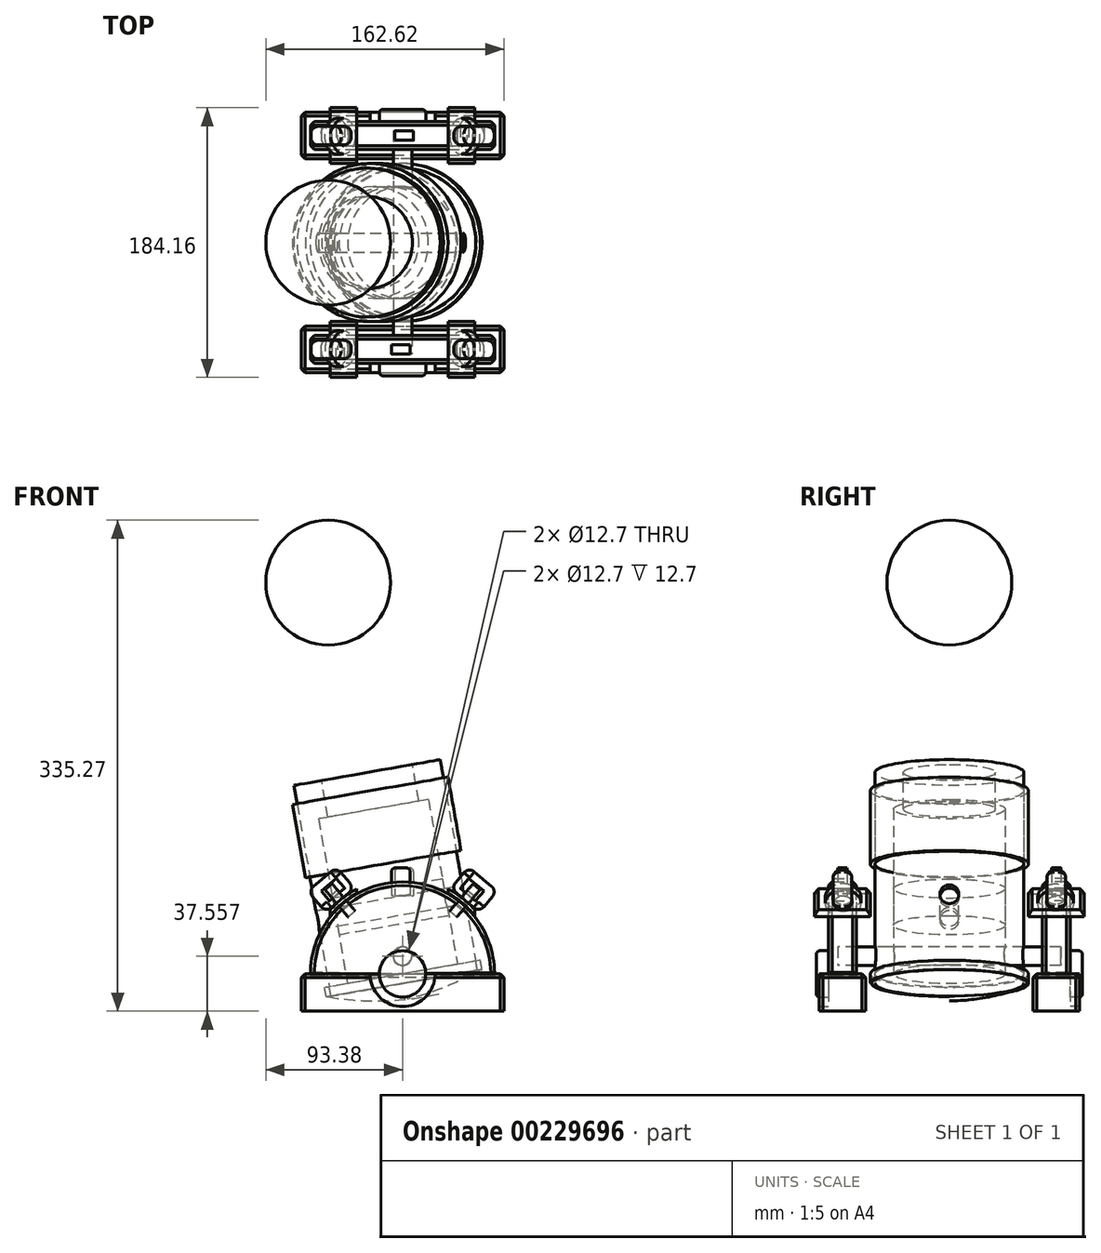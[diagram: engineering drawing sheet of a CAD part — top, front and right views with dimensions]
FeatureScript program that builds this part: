
annotation { "Feature Type Name" : "Feature", "Feature Type Description" : "" }
export const myFeature = defineFeature(function(context is Context, id is Id, definition is map)
    precondition{}
    {
        {
            var Q0;
            Q0=qCreatedBy(makeId("Top.planeOp"),FACE);
            var sketch = newSketch(context, id + "F0", { "sketchPlane" : qUnion([Q0])});
            skCircle(sketch, "E0", {"center": v(0, 0) * mm, "radius": 38.1 * mm});
            skCircle(sketch, "E1", {"center": v(0, 0) * mm, "radius": 50.8 * mm});
            skSolve(sketch);
        }
        {
            var Q0;
            Q0=makeQuery(id+"F0.imprint","IMPRINT",FACE,{"disambiguationData":[TD([[makeQuery(id+"F0.imprint","IMPRINT",EDGE,{"derivedFrom":sQuery(id+"F0.wireOp",EDGE,"E0")}),-1.0]])]});
            extrude(context, id + "F1", {"entities" : qUnion([Q0]), "depth" : 139.7 * mm});
        }
        {
            var Q0;
            Q0=qCreatedBy(makeId("Top.planeOp"),FACE);
            cPlane(context, id + "F2", {"entities" : qUnion([Q0]), "cplaneType" : CPlaneType.OFFSET, "offset" : 76.2 * mm, "width" : 152.4 * mm, "height" : 152.4 * mm});
        }
        {
            var Q0;
            Q0=qCreatedBy(id+"F2.planeOp",FACE);
            var sketch = newSketch(context, id + "F3", { "sketchPlane" : qUnion([Q0])});
            skCircle(sketch, "E2", {"center": v(0, 0) * mm, "radius": 50.8 * mm});
            skCircle(sketch, "E3", {"center": v(0, 0) * mm, "radius": 53.98 * mm});
            skSolve(sketch);
        }
        {
            var Q0;
            Q0=makeQuery(id+"F3.imprint","IMPRINT",FACE,{"disambiguationData":[TD([[makeQuery(id+"F3.imprint","IMPRINT",EDGE,{"derivedFrom":sQuery(id+"F3.wireOp",EDGE,"E2")}),-1.0]])]});
            extrude(context, id + "F4", {"entities" : qUnion([Q0]), "depth" : 50.8 * mm});
        }
        {
            var Q0;
            Q0=qCreatedBy(makeId("Front.planeOp"),FACE);
            cPlane(context, id + "F5", {"entities" : qUnion([Q0]), "cplaneType" : CPlaneType.OFFSET, "offset" : 63.5 * mm, "width" : 152.4 * mm, "height" : 152.4 * mm});
        }
        {
            var Q0;
            Q0=qCreatedBy(id+"F5.planeOp",FACE);
            var sketch = newSketch(context, id + "F6", { "sketchPlane" : qUnion([Q0])});
            skArc(sketch, "E4", {"start": v(45.28, -43.66) * mm, "mid": v(43.66, 45.28) * mm, "end": v(-45.28, 43.66) * mm});
            skLineSegment(sketch, "E5", {"start": v(-45.28, 43.66) * mm, "end": v(45.28, -43.66) * mm});
            skSolve(sketch);
        }
        {
            var Q0;
            Q0 = qSketchRegion(id + "F6", true);
            extrude(context, id + "F7", {"entities" : qUnion([Q0]), "depth" : 19.05 * mm});
        }
        {
            var Q0;
            Q0=qCreatedBy(makeId("Top.planeOp"),FACE);
            var sketch = newSketch(context, id + "F8", { "sketchPlane" : qUnion([Q0])});
            skLineSegment(sketch, "E6", {"start": v(0, 0) * mm, "end": v(0, -70.78) * mm});
            skSolve(sketch);
        }
        {
            var Q0;
            Q0=makeQuery(id+"F7.opExtrude","SWEPT_BODY",BODY,{"disambiguationData":[OSD([sQuery(id+"F6.wireOp",EDGE,"E4"),sQuery(id+"F6.wireOp",EDGE,"E5")])]});
            var Q1;
            Q1=sQuery(id+"F8.wireOp",EDGE,"E6");
            transform(context, id + "F9", {"entities" : qUnion([Q0]), "transformType" : TransformType.ROTATION, "transformAxis" : qUnion([Q1]), "angle" : 45 * degree, "makeCopy" : false});
        }
        {
            var Q0;
            Q0=qCreatedBy(makeId("Top.planeOp"),FACE);
            var sketch = newSketch(context, id + "F10", { "sketchPlane" : qUnion([Q0])});
            skLineSegment(sketch, "E7.0.0", {"start": v(-62.9, -63.5) * mm, "end": v(62.9, -63.5) * mm});
            skLineSegment(sketch, "E7.0.1", {"start": v(62.9, -63.5) * mm, "end": v(62.9, -82.55) * mm});
            skLineSegment(sketch, "E7.0.2", {"start": v(62.9, -82.55) * mm, "end": v(-62.9, -82.55) * mm});
            skLineSegment(sketch, "E7.0.3", {"start": v(-62.9, -82.55) * mm, "end": v(-62.9, -63.5) * mm});
            skLineSegment(sketch, "E8", {"start": v(-62.9, -82.55) * mm, "end": v(-69.24, -82.55) * mm});
            skLineSegment(sketch, "E9", {"start": v(-62.9, -82.55) * mm, "end": v(-62.9, -88.9) * mm});
            skLineSegment(sketch, "E10.MirrorCS", {"start": v(62.9, -82.55) * mm, "end": v(62.9, -88.9) * mm});
            skLineSegment(sketch, "E11.MirrorCS", {"start": v(62.9, -82.55) * mm, "end": v(69.24, -82.55) * mm});
            skLineSegment(sketch, "E12", {"start": v(62.9, -63.5) * mm, "end": v(62.9, -57.15) * mm});
            skLineSegment(sketch, "E13", {"start": v(62.9, -63.5) * mm, "end": v(69.24, -63.5) * mm});
            skLineSegment(sketch, "E14.bottom", {"start": v(-69.24, -88.9) * mm, "end": v(69.24, -88.9) * mm});
            skLineSegment(sketch, "E14.top", {"start": v(-69.24, -57.15) * mm, "end": v(69.24, -57.15) * mm});
            skLineSegment(sketch, "E14.left", {"start": v(-69.24, -88.9) * mm, "end": v(-69.24, -57.15) * mm});
            skLineSegment(sketch, "E14.right", {"start": v(69.24, -88.9) * mm, "end": v(69.24, -57.15) * mm});
            skSolve(sketch);
        }
        {
            var Q0;
            {var subQ0=sQuery(id+"F10.wireOp",EDGE,"E12");Q0=makeQuery(id+"F10.imprint","IMPRINT",FACE,{"disambiguationData":[TD([[makeQuery(id+"F10.imprint","IMPRINT",EDGE,{"derivedFrom":subQ0}),-1.0]])]});}
            var Q1;
            Q1=makeQuery(id+"F10.imprint","IMPRINT",FACE,{"disambiguationData":[TD([[makeQuery(id+"F10.imprint","IMPRINT",EDGE,{"derivedFrom":sQuery(id+"F10.wireOp",EDGE,"E7.0.1")}),1.0]])]});
            var Q2;
            Q2=makeQuery(id+"F10.imprint","IMPRINT",FACE,{"disambiguationData":[TD([[makeQuery(id+"F10.imprint","IMPRINT",EDGE,{"derivedFrom":sQuery(id+"F10.wireOp",EDGE,"E7.0.0")}),-1.0]])]});
            var Q3;
            Q3=makeQuery(id+"F10.imprint","IMPRINT",FACE,{"disambiguationData":[TD([[makeQuery(id+"F10.imprint","IMPRINT",EDGE,{"derivedFrom":sQuery(id+"F10.wireOp",EDGE,"E7.0.0")}),1.0]])]});
            var Q4;
            {var subQ0=sQuery(id+"F10.wireOp",EDGE,"E11.MirrorCS");Q4=makeQuery(id+"F10.imprint","IMPRINT",FACE,{"disambiguationData":[TD([[makeQuery(id+"F10.imprint","IMPRINT",EDGE,{"derivedFrom":subQ0}),-1.0]])]});}
            var Q5;
            Q5=makeQuery(id+"F10.imprint","IMPRINT",FACE,{"disambiguationData":[TD([[makeQuery(id+"F10.imprint","IMPRINT",EDGE,{"derivedFrom":sQuery(id+"F10.wireOp",EDGE,"E7.0.2")}),1.0]])]});
            var Q6;
            {var subQ0=sQuery(id+"F10.wireOp",EDGE,"E8");Q6=makeQuery(id+"F10.imprint","IMPRINT",FACE,{"disambiguationData":[TD([[makeQuery(id+"F10.imprint","IMPRINT",EDGE,{"derivedFrom":subQ0}),1.0]])]});}
            extrude(context, id + "F11", {"entities" : qUnion([Q0, Q1, Q2, Q3, Q4, Q5, Q6]), "oppositeDirection" : true, "depth" : 25.4 * mm});
        }
        {
            var Q0;
            Q0=makeQuery(id+"F7.opExtrude","CAP_FACE",FACE,{"disambiguationData":[OSD([sQuery(id+"F6.wireOp",EDGE,"E4"),sQuery(id+"F6.wireOp",EDGE,"E5")])],"isStart":false});
            var sketch = newSketch(context, id + "F12", { "sketchPlane" : qUnion([Q0])});
            skCircle(sketch, "E15", {"center": v(0, 0) * mm, "radius": 22.23 * mm});
            skCircle(sketch, "E16", {"center": v(0, 0) * mm, "radius": 15.88 * mm});
            skSolve(sketch);
        }
        {
            var Q0;
            {var subQ0=sQuery(id+"F12.wireOp",EDGE,"E16");var subQ1=makeQuery(id+"F7.opExtrude","CAP_EDGE",EDGE,{"disambiguationData":[OSD([sQuery(id+"F6.wireOp",EDGE,"E5")])],"isStart":false});var subQ2=makeQuery(id+"F12.imprint","INTERSECT",VERTEX,{"disambiguationData":[OD(0.0)],"derivedFrom":[subQ1,subQ0]});Q0=makeQuery(id+"F12.imprint","IMPRINT",FACE,{"disambiguationData":[TD([[makeQuery(id+"F12.imprint","IMPRINT",EDGE,{"disambiguationData":[TD([[subQ2,-1.0]])],"derivedFrom":subQ0}),1.0]])]});}
            var Q1;
            {var subQ0=sQuery(id+"F12.wireOp",EDGE,"E16");var subQ1=makeQuery(id+"F7.opExtrude","CAP_EDGE",EDGE,{"disambiguationData":[OSD([sQuery(id+"F6.wireOp",EDGE,"E5")])],"isStart":false});var subQ2=makeQuery(id+"F12.imprint","INTERSECT",VERTEX,{"disambiguationData":[OD(0.0)],"derivedFrom":[subQ1,subQ0]});Q1=makeQuery(id+"F12.imprint","IMPRINT",FACE,{"disambiguationData":[TD([[makeQuery(id+"F12.imprint","IMPRINT",EDGE,{"disambiguationData":[TD([[subQ2,1.0]])],"derivedFrom":subQ0}),1.0]])]});}
            extrude(context, id + "F13", {"entities" : qUnion([Q0, Q1]), "depth" : 8.38 * mm});
        }
        {
            var Q0;
            {var subQ0=sQuery(id+"F12.wireOp",EDGE,"E15");var subQ1=makeQuery(id+"F7.opExtrude","CAP_EDGE",EDGE,{"disambiguationData":[OSD([sQuery(id+"F6.wireOp",EDGE,"E5")])],"isStart":false});var subQ2=makeQuery(id+"F12.imprint","INTERSECT",VERTEX,{"disambiguationData":[OD(0.0)],"derivedFrom":[subQ1,subQ0]});Q0=makeQuery(id+"F12.imprint","IMPRINT",FACE,{"disambiguationData":[TD([[makeQuery(id+"F12.imprint","IMPRINT",EDGE,{"disambiguationData":[TD([[subQ2,-1.0]])],"derivedFrom":subQ0}),1.0]])]});}
            var Q1;
            {var subQ0=sQuery(id+"F12.wireOp",EDGE,"E15");var subQ1=makeQuery(id+"F7.opExtrude","CAP_EDGE",EDGE,{"disambiguationData":[OSD([sQuery(id+"F6.wireOp",EDGE,"E5")])],"isStart":false});var subQ2=makeQuery(id+"F12.imprint","INTERSECT",VERTEX,{"disambiguationData":[OD(0.0)],"derivedFrom":[subQ1,subQ0]});Q1=makeQuery(id+"F12.imprint","IMPRINT",FACE,{"disambiguationData":[TD([[makeQuery(id+"F12.imprint","IMPRINT",EDGE,{"disambiguationData":[TD([[subQ2,1.0]])],"derivedFrom":subQ0}),1.0]])]});}
            extrude(context, id + "F14", {"entities" : qUnion([Q0, Q1]), "depth" : 6.35 * mm});
        }
        {
            var Q0;
            Q0=makeQuery(id+"F14.opExtrude","CAP_EDGE",EDGE,{"disambiguationData":[OSD([sQuery(id+"F12.wireOp",EDGE,"E15")])],"isStart":false});
            var Q1;
            Q1=makeQuery(id+"F13.opExtrude","CAP_EDGE",EDGE,{"disambiguationData":[OSD([sQuery(id+"F12.wireOp",EDGE,"E16")])],"isStart":false});
            fillet(context, id + "F15", {"entities" : qUnion([Q0, Q1]), "radius" : 2.54 * mm, "tangentPropagation" : true, "allowEdgeOverflow" : false});
        }
        {
            var Q0;
            Q0 = qSketchRegion(id + "F12", true);
            var Q1;
            Q1=sQuery(id+"F12.wireOp",EDGE,"E15");
            extrude(context, id + "F16", {"entities" : qUnion([Q0]), "operationType" : NewBodyOperationType.REMOVE, "surfaceEntities" : qUnion([Q1]), "depth" : 25.4 * mm});
        }
        {
            var Q0;
            Q0=makeQuery(id+"F7.opExtrude","SWEPT_BODY",BODY,{"disambiguationData":[OSD([sQuery(id+"F6.wireOp",EDGE,"E4"),sQuery(id+"F6.wireOp",EDGE,"E5")])]});
            var Q1;
            Q1=makeQuery(id+"F13.opExtrude","SWEPT_BODY",BODY,{"disambiguationData":[OSD([sQuery(id+"F12.wireOp",EDGE,"E16")])]});
            var Q2;
            Q2=makeQuery(id+"F14.opExtrude","SWEPT_BODY",BODY,{"disambiguationData":[OSD([sQuery(id+"F12.wireOp",EDGE,"E15"),sQuery(id+"F12.wireOp",EDGE,"E16")])]});
            var Q3;
            Q3=makeQuery(id+"F16.boolean.opBoolean","SPLIT",BODY,{"disambiguationData":[OD(0.0)],"derivedFrom":makeQuery(id+"F11.opExtrude","SWEPT_BODY",BODY,{"disambiguationData":[OSD([sQuery(id+"F10.wireOp",EDGE,"E7.0.0"),sQuery(id+"F10.wireOp",EDGE,"E7.0.1"),sQuery(id+"F10.wireOp",EDGE,"E7.0.2"),sQuery(id+"F10.wireOp",EDGE,"E7.0.3"),sQuery(id+"F10.wireOp",EDGE,"E14.bottom"),sQuery(id+"F10.wireOp",EDGE,"E14.top"),sQuery(id+"F10.wireOp",EDGE,"E14.left"),sQuery(id+"F10.wireOp",EDGE,"E14.right")])]})});
            var Q4;
            Q4=makeQuery(id+"F16.boolean.opBoolean","SPLIT",BODY,{"disambiguationData":[OD(1.0)],"derivedFrom":makeQuery(id+"F11.opExtrude","SWEPT_BODY",BODY,{"disambiguationData":[OSD([sQuery(id+"F10.wireOp",EDGE,"E7.0.0"),sQuery(id+"F10.wireOp",EDGE,"E7.0.1"),sQuery(id+"F10.wireOp",EDGE,"E7.0.2"),sQuery(id+"F10.wireOp",EDGE,"E7.0.3"),sQuery(id+"F10.wireOp",EDGE,"E14.bottom"),sQuery(id+"F10.wireOp",EDGE,"E14.top"),sQuery(id+"F10.wireOp",EDGE,"E14.left"),sQuery(id+"F10.wireOp",EDGE,"E14.right")])]})});
            var Q5;
            Q5=makeQuery(id+"F1.opExtrude","SWEPT_FACE",FACE,{"disambiguationData":[OSD([sQuery(id+"F0.wireOp",EDGE,"E0")])]});
            transform(context, id + "F17", {"entities" : qUnion([Q0, Q1, Q2, Q3, Q4]), "transformType" : TransformType.ROTATION, "transformAxis" : qUnion([Q5]), "angle" : 180 * degree, "makeCopy" : true});
        }
        {
            var Q0;
            Q0=makeQuery(id+"F17.opPattern","COPY",BODY,{"derivedFrom":makeQuery(id+"F7.opExtrude","SWEPT_BODY",BODY,{"disambiguationData":[OSD([sQuery(id+"F6.wireOp",EDGE,"E4"),sQuery(id+"F6.wireOp",EDGE,"E5")])]}),"instanceName":"1"});
            var Q1;
            Q1=makeQuery(id+"F17.opPattern","COPY",BODY,{"derivedFrom":makeQuery(id+"F13.opExtrude","SWEPT_BODY",BODY,{"disambiguationData":[OSD([sQuery(id+"F12.wireOp",EDGE,"E16")])]}),"instanceName":"1"});
            var Q2;
            Q2=makeQuery(id+"F17.opPattern","COPY",BODY,{"derivedFrom":makeQuery(id+"F14.opExtrude","SWEPT_BODY",BODY,{"disambiguationData":[OSD([sQuery(id+"F12.wireOp",EDGE,"E15"),sQuery(id+"F12.wireOp",EDGE,"E16")])]}),"instanceName":"1"});
            var Q3;
            Q3=makeQuery(id+"F17.opPattern","COPY",BODY,{"derivedFrom":makeQuery(id+"F16.boolean.opBoolean","SPLIT",BODY,{"disambiguationData":[OD(0.0)],"derivedFrom":makeQuery(id+"F11.opExtrude","SWEPT_BODY",BODY,{"disambiguationData":[OSD([sQuery(id+"F10.wireOp",EDGE,"E7.0.0"),sQuery(id+"F10.wireOp",EDGE,"E7.0.1"),sQuery(id+"F10.wireOp",EDGE,"E7.0.2"),sQuery(id+"F10.wireOp",EDGE,"E7.0.3"),sQuery(id+"F10.wireOp",EDGE,"E14.bottom"),sQuery(id+"F10.wireOp",EDGE,"E14.top"),sQuery(id+"F10.wireOp",EDGE,"E14.left"),sQuery(id+"F10.wireOp",EDGE,"E14.right")])]})}),"instanceName":"1"});
            var Q4;
            Q4=makeQuery(id+"F17.opPattern","COPY",BODY,{"derivedFrom":makeQuery(id+"F16.boolean.opBoolean","SPLIT",BODY,{"disambiguationData":[OD(1.0)],"derivedFrom":makeQuery(id+"F11.opExtrude","SWEPT_BODY",BODY,{"disambiguationData":[OSD([sQuery(id+"F10.wireOp",EDGE,"E7.0.0"),sQuery(id+"F10.wireOp",EDGE,"E7.0.1"),sQuery(id+"F10.wireOp",EDGE,"E7.0.2"),sQuery(id+"F10.wireOp",EDGE,"E7.0.3"),sQuery(id+"F10.wireOp",EDGE,"E14.bottom"),sQuery(id+"F10.wireOp",EDGE,"E14.top"),sQuery(id+"F10.wireOp",EDGE,"E14.left"),sQuery(id+"F10.wireOp",EDGE,"E14.right")])]})}),"instanceName":"1"});
            deleteBodies(context, id + "F18", {"entities" : qUnion([Q0, Q1, Q2, Q3, Q4])});
        }
        {
            var Q0;
            {var subQ1=sQuery(id+"F10.wireOp",EDGE,"E14.left");var subQ3=sQuery(id+"F10.wireOp",EDGE,"E14.bottom");Q0=makeQuery(id+"F16.boolean.opBoolean","SPLIT",FACE,{"disambiguationData":[TD([makeQuery(id+"F11.opExtrude","SWEPT_FACE",FACE,{"disambiguationData":[OSD([subQ1])]})])],"derivedFrom":makeQuery(id+"F11.opExtrude","SWEPT_FACE",FACE,{"disambiguationData":[OSD([subQ3])]})});}
            cPlane(context, id + "F19", {"entities" : qUnion([Q0]), "cplaneType" : CPlaneType.OFFSET, "offset" : 3.17 * mm, "width" : 152.4 * mm, "height" : 152.4 * mm});
        }
        {
            var Q0;
            Q0=qCreatedBy(id+"F19.planeOp",FACE);
            var sketch = newSketch(context, id + "F20", { "sketchPlane" : qUnion([Q0])});
            skArc(sketch, "E17.0", {"start": v(62.9, 1.15) * mm, "mid": v(-1.15, 62.9) * mm, "end": v(-62.9, -1.15) * mm});
            skLineSegment(sketch, "E18.0", {"start": v(-69.24, -25.4) * mm, "end": v(69.24, -25.4) * mm});
            skLineSegment(sketch, "E19", {"start": v(-49.3, -25.4) * mm, "end": v(-49.3, 43.8) * mm});
            skLineSegment(sketch, "E20", {"start": v(-49.3, -25.4) * mm, "end": v(-31.25, -25.4) * mm});
            skLineSegment(sketch, "E21", {"start": v(-31.25, -25.4) * mm, "end": v(-31.25, 58.08) * mm});
            skArc(sketch, "E22", {"start": v(-31.25, 58.08) * mm, "mid": v(-40.9, 51.74) * mm, "end": v(-49.3, 43.8) * mm});
            skArc(sketch, "E23.trimOffspring", {"start": v(-60.86, -25.4) * mm, "mid": v(0, -65.95) * mm, "end": v(60.86, -25.4) * mm});
            skSolve(sketch);
        }
        {
            var Q0;
            {var subQ5=sQuery(id+"F20.wireOp",EDGE,"E20");Q0=makeQuery(id+"F20.imprint","IMPRINT",FACE,{"disambiguationData":[TD([[makeQuery(id+"F20.imprint","IMPRINT",EDGE,{"derivedFrom":subQ5}),1.0]])]});}
            var Q1;
            {var subQ5=sQuery(id+"F20.wireOp",EDGE,"E22");Q1=makeQuery(id+"F20.imprint","IMPRINT",FACE,{"disambiguationData":[TD([[makeQuery(id+"F20.imprint","IMPRINT",EDGE,{"derivedFrom":subQ5}),1.0]])]});}
            extrude(context, id + "F21", {"entities" : qUnion([Q0, Q1]), "oppositeDirection" : true, "depth" : 38.1 * mm});
        }
        {
            var Q0;
            Q0=makeQuery(id+"F7.opExtrude","CAP_FACE",FACE,{"disambiguationData":[OSD([sQuery(id+"F6.wireOp",EDGE,"E4"),sQuery(id+"F6.wireOp",EDGE,"E5")])],"isStart":false});
            cPlane(context, id + "F22", {"entities" : qUnion([Q0]), "cplaneType" : CPlaneType.OFFSET, "offset" : 9.52 * mm, "oppositeDirection" : true, "width" : 152.4 * mm, "height" : 152.4 * mm});
        }
        {
            var Q0;
            Q0=qCreatedBy(id+"F22.planeOp",FACE);
            var sketch = newSketch(context, id + "F23", { "sketchPlane" : qUnion([Q0])});
            skPoint(sketch, "E24.0", {"position": v(-1.15, 62.9) * mm});
            skLineSegment(sketch, "E25.bottom", {"start": v(5.2, 72.42) * mm, "end": v(-7.5, 72.42) * mm});
            skLineSegment(sketch, "E25.top", {"start": v(5.2, 53.37) * mm, "end": v(-7.5, 53.37) * mm});
            skLineSegment(sketch, "E25.left", {"start": v(5.2, 72.42) * mm, "end": v(5.2, 53.37) * mm});
            skLineSegment(sketch, "E25.right", {"start": v(-7.5, 72.42) * mm, "end": v(-7.5, 53.37) * mm});
            skSolve(sketch);
        }
        {
            var Q0;
            Q0=makeQuery(id+"F23.imprint","IMPRINT",FACE,{"disambiguationData":[TD([[makeQuery(id+"F23.imprint","IMPRINT",EDGE,{"derivedFrom":sQuery(id+"F23.wireOp",EDGE,"E25.bottom")}),1.0]])]});
            extrude(context, id + "F24", {"entities" : qUnion([Q0]), "depth" : 6.35 * mm, "symmetric" : true});
        }
        {
            var Q0;
            Q0=makeQuery(id+"F24.opExtrude","SWEPT_EDGE",EDGE,{"disambiguationData":[OSD([sQuery(id+"F23.wireOp",EDGE,"E25.bottom"),sQuery(id+"F23.wireOp",EDGE,"E25.right")])]});
            var Q1;
            Q1=makeQuery(id+"F24.opExtrude","SWEPT_EDGE",EDGE,{"disambiguationData":[OSD([sQuery(id+"F23.wireOp",EDGE,"E25.bottom"),sQuery(id+"F23.wireOp",EDGE,"E25.left")])]});
            fillet(context, id + "F25", {"entities" : qUnion([Q0, Q1]), "radius" : 2.54 * mm, "tangentPropagation" : true, "allowEdgeOverflow" : false});
        }
        {
            var Q0;
            Q0=makeQuery(id+"F21.opExtrude","CAP_EDGE",EDGE,{"disambiguationData":[OSD([sQuery(id+"F20.wireOp",EDGE,"E22")])],"isStart":true});
            var Q1;
            Q1=makeQuery(id+"FDD8fb37NUxeniG_7.opPattern","COPY",EDGE,{"derivedFrom":makeQuery(id+"F21.opExtrude","CAP_EDGE",EDGE,{"disambiguationData":[OSD([sQuery(id+"F20.wireOp",EDGE,"E22")])],"isStart":true}),"instanceName":"1"});
            var Q2;
            {var subQ0=sQuery(id+"F10.wireOp",EDGE,"E14.left");var subQ1=sQuery(id+"F10.wireOp",EDGE,"E14.bottom");Q2=makeQuery(id+"F16.boolean.opBoolean","SPLIT",EDGE,{"disambiguationData":[TD([makeQuery(id+"F11.opExtrude","SWEPT_FACE",FACE,{"disambiguationData":[OSD([subQ0])]})])],"derivedFrom":makeQuery(id+"F11.opExtrude","CAP_EDGE",EDGE,{"disambiguationData":[OSD([subQ1])],"isStart":true})});}
            var Q3;
            {var subQ0=sQuery(id+"F10.wireOp",EDGE,"E14.right");var subQ1=sQuery(id+"F10.wireOp",EDGE,"E14.bottom");Q3=makeQuery(id+"F16.boolean.opBoolean","SPLIT",EDGE,{"disambiguationData":[TD([makeQuery(id+"F11.opExtrude","SWEPT_FACE",FACE,{"disambiguationData":[OSD([subQ0])]})])],"derivedFrom":makeQuery(id+"F11.opExtrude","CAP_EDGE",EDGE,{"disambiguationData":[OSD([subQ1])],"isStart":true})});}
            var Q4;
            Q4=makeQuery(id+"F11.opExtrude","CAP_EDGE",EDGE,{"disambiguationData":[OSD([sQuery(id+"F10.wireOp",EDGE,"E14.left")])],"isStart":true});
            var Q5;
            Q5=makeQuery(id+"F11.opExtrude","SWEPT_EDGE",EDGE,{"disambiguationData":[OSD([sQuery(id+"F10.wireOp",EDGE,"E14.bottom"),sQuery(id+"F10.wireOp",EDGE,"E14.left")])]});
            var Q6;
            Q6=makeQuery(id+"F21.opExtrude","CAP_EDGE",EDGE,{"disambiguationData":[OSD([sQuery(id+"F20.wireOp",EDGE,"E22")])],"isStart":false});
            var Q7;
            Q7=makeQuery(id+"F7.opExtrude","CAP_EDGE",EDGE,{"disambiguationData":[OSD([sQuery(id+"F6.wireOp",EDGE,"E4")])],"isStart":false});
            var Q8;
            Q8=makeQuery(id+"F7.opExtrude","CAP_EDGE",EDGE,{"disambiguationData":[OSD([sQuery(id+"F6.wireOp",EDGE,"E4")])],"isStart":true});
            var Q9;
            Q9=makeQuery(id+"F11.opExtrude","CAP_EDGE",EDGE,{"disambiguationData":[OSD([sQuery(id+"F10.wireOp",EDGE,"E14.top")])],"isStart":true});
            var Q10;
            Q10=makeQuery(id+"F11.opExtrude","SWEPT_EDGE",EDGE,{"disambiguationData":[OSD([sQuery(id+"F10.wireOp",EDGE,"E14.top"),sQuery(id+"F10.wireOp",EDGE,"E14.left")])]});
            var Q11;
            Q11=makeQuery(id+"F11.opExtrude","SWEPT_EDGE",EDGE,{"disambiguationData":[OSD([sQuery(id+"F10.wireOp",EDGE,"E14.bottom"),sQuery(id+"F10.wireOp",EDGE,"E14.right")])]});
            var Q12;
            Q12=makeQuery(id+"F11.opExtrude","CAP_EDGE",EDGE,{"disambiguationData":[OSD([sQuery(id+"F10.wireOp",EDGE,"E14.right")])],"isStart":true});
            var Q13;
            Q13=makeQuery(id+"FDD8fb37NUxeniG_7.opPattern","COPY",EDGE,{"derivedFrom":makeQuery(id+"F21.opExtrude","CAP_EDGE",EDGE,{"disambiguationData":[OSD([sQuery(id+"F20.wireOp",EDGE,"E22")])],"isStart":false}),"instanceName":"1"});
            var Q14;
            Q14=makeQuery(id+"F11.opExtrude","SWEPT_EDGE",EDGE,{"disambiguationData":[OSD([sQuery(id+"F10.wireOp",EDGE,"E14.top"),sQuery(id+"F10.wireOp",EDGE,"E14.right")])]});
            chamfer(context, id + "F26", {"entities" : qUnion([Q0, Q1, Q2, Q3, Q4, Q5, Q6, Q7, Q8, Q9, Q10, Q11, Q12, Q13, Q14]), "width" : 2.54 * mm, "tangentPropagation" : true});
        }
        {
            var Q0;
            {var subQ0=sQuery(id+"F20.wireOp",EDGE,"E22");Q0=makeQuery(id+"F26.opChamfer","BLEND_EDGE",EDGE,{"blendedFrom":[makeQuery(id+"F21.opExtrude","CAP_EDGE",EDGE,{"disambiguationData":[OSD([subQ0])],"isStart":true}),makeQuery(id+"F21.opExtrude","CAP_FACE",FACE,{"disambiguationData":[OSD([sQuery(id+"F20.wireOp",EDGE,"E19"),sQuery(id+"F20.wireOp",EDGE,"E21"),subQ0,sQuery(id+"F20.wireOp",EDGE,"E20")])],"isStart":true})],"blendedInto":[makeQuery(id+"F21.opExtrude","CAP_FACE",FACE,{"disambiguationData":[OSD([sQuery(id+"F20.wireOp",EDGE,"E19"),sQuery(id+"F20.wireOp",EDGE,"E21"),subQ0,sQuery(id+"F20.wireOp",EDGE,"E20")])],"isStart":true})]});}
            cPoint(context, id + "F27", {"entities" : qUnion([Q0]), "parameter" : 0.5});
        }
        {
            var Q0;
            {var subQ0=sQuery(id+"F6.wireOp",EDGE,"E4");Q0=makeQuery(id+"F26.opChamfer","BLEND_EDGE",EDGE,{"blendedFrom":[makeQuery(id+"F7.opExtrude","CAP_EDGE",EDGE,{"disambiguationData":[OSD([subQ0])],"isStart":false}),makeQuery(id+"F7.opExtrude","SWEPT_FACE",FACE,{"disambiguationData":[OSD([subQ0])]})],"blendedInto":[makeQuery(id+"F7.opExtrude","SWEPT_FACE",FACE,{"disambiguationData":[OSD([subQ0])]})]});}
            var Q1;
            Q1 = qCreatedBy(id + "F27" ,VERTEX);
            cPlane(context, id + "F28", {"entities" : qUnion([Q0, Q1]), "cplaneType" : CPlaneType.CURVE_POINT, "offset" : 25.4 * mm, "width" : 152.4 * mm, "height" : 152.4 * mm});
        }
        {
            var Q0;
            Q0=qCreatedBy(id+"F28.planeOp",FACE);
            var sketch = newSketch(context, id + "F29", { "sketchPlane" : qUnion([Q0])});
            skLineSegment(sketch, "E26", {"start": v(-76.83, 65.95) * mm, "end": v(-68.32, 65.95) * mm});
            skCircle(sketch, "E27", {"center": v(-72.58, 65.95) * mm, "radius": 12.21 * mm});
            skCircle(sketch, "E28", {"center": v(-72.58, 65.95) * mm, "radius": 6.35 * mm});
            skSolve(sketch);
        }
        {
            var Q0;
            {var subQ0=sQuery(id+"F29.wireOp",EDGE,"E27");var subQ1=sQuery(id+"F29.wireOp",EDGE,"E26");var subQ2=makeQuery(id+"F29.imprint","INTERSECT",VERTEX,{"disambiguationData":[OD(0.0)],"derivedFrom":[subQ1,subQ0]});Q0=makeQuery(id+"F29.imprint","IMPRINT",FACE,{"disambiguationData":[TD([[makeQuery(id+"F29.imprint","IMPRINT",EDGE,{"disambiguationData":[TD([[subQ2,-1.0]])],"derivedFrom":subQ1}),1.0]])]});}
            var Q1;
            Q1=makeQuery(id+"F29.imprint","IMPRINT",FACE,{"disambiguationData":[TD([[makeQuery(id+"F29.imprint","IMPRINT",EDGE,{"derivedFrom":sQuery(id+"F29.wireOp",EDGE,"E27")}),1.0]])]});
            extrude(context, id + "F30", {"entities" : qUnion([Q0, Q1]), "depth" : 6.35 * mm, "symmetric" : true});
        }
        {
            var Q0;
            Q0=qCreatedBy(id+"F28.planeOp",FACE);
            var sketch = newSketch(context, id + "F31", { "sketchPlane" : qUnion([Q0])});
            skLineSegment(sketch, "E29.0", {"start": v(-66.23, 65.95) * mm, "end": v(-66.23, 65.95) * mm});
            skCircle(sketch, "E30", {"center": v(-72.58, 65.95) * mm, "radius": 6.35 * mm});
            skSolve(sketch);
        }
        {
            var Q0;
            Q0=qCreatedBy(id+"F22.planeOp",FACE);
            var sketch = newSketch(context, id + "F32", { "sketchPlane" : qUnion([Q0])});
            skLineSegment(sketch, "E31.0", {"start": v(-46.74, 55.16) * mm, "end": v(-38.53, 45.47) * mm});
            skLineSegment(sketch, "E32", {"start": v(-42.63, 50.32) * mm, "end": v(-52.32, 42.1) * mm});
            skLineSegment(sketch, "E33", {"start": v(-41.15, 68.22) * mm, "end": v(-41.15, 68.22) * mm});
            skPoint(sketch, "E34.startSnap0", {"position": v(-41.15, 68.22) * mm});
            skLineSegment(sketch, "E35", {"start": v(-42.63, 50.32) * mm, "end": v(-32.94, 58.53) * mm});
            skLineSegment(sketch, "E36", {"start": v(-32.94, 58.53) * mm, "end": v(-45.26, 73.06) * mm});
            skLineSegment(sketch, "E37", {"start": v(-45.26, 73.06) * mm, "end": v(-64.64, 56.64) * mm});
            skLineSegment(sketch, "E38", {"start": v(-64.64, 56.64) * mm, "end": v(-52.32, 42.1) * mm});
            skLineSegment(sketch, "E39", {"start": v(-42.63, 50.32) * mm, "end": v(-44.18, 52.14) * mm});
            skLineSegment(sketch, "E40", {"start": v(-55.52, 56.64) * mm, "end": v(-45.26, 65.34) * mm});
            skLineSegment(sketch, "E41", {"start": v(-45.26, 65.34) * mm, "end": v(-39.49, 58.53) * mm});
            skLineSegment(sketch, "E42", {"start": v(-39.49, 58.53) * mm, "end": v(-49.75, 49.83) * mm});
            skPoint(sketch, "E42.endSnap0", {"position": v(-47.48, 46.21) * mm});
            skLineSegment(sketch, "E43", {"start": v(-49.75, 49.83) * mm, "end": v(-55.52, 56.64) * mm});
            skSolve(sketch);
        }
        {
            var Q0;
            Q0=makeQuery(id+"F32.imprint","IMPRINT",FACE,{"disambiguationData":[TD([[makeQuery(id+"F32.imprint","IMPRINT",EDGE,{"derivedFrom":sQuery(id+"F32.wireOp",EDGE,"E32")}),-1.0]])]});
            extrude(context, id + "F33", {"entities" : qUnion([Q0]), "depth" : 12.7 * mm, "symmetric" : true});
        }
        {
            var Q0;
            Q0=makeQuery(id+"F33.opExtrude","SWEPT_EDGE",EDGE,{"disambiguationData":[OSD([sQuery(id+"F32.wireOp",EDGE,"E37"),sQuery(id+"F32.wireOp",EDGE,"E38")])]});
            var Q1;
            Q1=makeQuery(id+"F33.opExtrude","SWEPT_EDGE",EDGE,{"disambiguationData":[OSD([sQuery(id+"F32.wireOp",EDGE,"E36"),sQuery(id+"F32.wireOp",EDGE,"E37")])]});
            var Q2;
            Q2=makeQuery(id+"F33.opExtrude","SWEPT_EDGE",EDGE,{"disambiguationData":[OSD([sQuery(id+"F32.wireOp",EDGE,"E32"),sQuery(id+"F32.wireOp",EDGE,"E38")])]});
            var Q3;
            Q3=makeQuery(id+"F33.opExtrude","SWEPT_EDGE",EDGE,{"disambiguationData":[OSD([sQuery(id+"F32.wireOp",EDGE,"E35"),sQuery(id+"F32.wireOp",EDGE,"E36")])]});
            var Q4;
            Q4=makeQuery(id+"F33.opExtrude","CAP_EDGE",EDGE,{"disambiguationData":[OSD([sQuery(id+"F32.wireOp",EDGE,"E37")])],"isStart":false});
            var Q5;
            Q5=makeQuery(id+"F33.opExtrude","CAP_EDGE",EDGE,{"disambiguationData":[OSD([sQuery(id+"F32.wireOp",EDGE,"E37")])],"isStart":true});
            var Q6;
            Q6=makeQuery(id+"F33.opExtrude","CAP_EDGE",EDGE,{"disambiguationData":[OSD([sQuery(id+"F32.wireOp",EDGE,"E38")])],"isStart":false});
            var Q7;
            Q7=makeQuery(id+"F33.opExtrude","CAP_EDGE",EDGE,{"disambiguationData":[OSD([sQuery(id+"F32.wireOp",EDGE,"E38")])],"isStart":true});
            fillet(context, id + "F34", {"entities" : qUnion([Q0, Q1, Q2, Q3, Q4, Q5, Q6, Q7]), "radius" : 5.08 * mm, "tangentPropagation" : true, "allowEdgeOverflow" : false});
        }
        {
            var Q0;
            {var subQ0=sQuery(id+"F32.wireOp",EDGE,"E36");var subQ1=sQuery(id+"F32.wireOp",EDGE,"E35");Q0=makeQuery(id+"F34.opFillet","BLEND_EDGE",EDGE,{"blendedFrom":[makeQuery(id+"F33.opExtrude","SWEPT_EDGE",EDGE,{"disambiguationData":[OSD([subQ1,subQ0])]}),makeQuery(id+"F33.opExtrude","CAP_FACE",FACE,{"disambiguationData":[OSD([sQuery(id+"F32.wireOp",EDGE,"E32"),subQ1,subQ0,sQuery(id+"F32.wireOp",EDGE,"E37"),sQuery(id+"F32.wireOp",EDGE,"E38"),sQuery(id+"F32.wireOp",EDGE,"E40"),sQuery(id+"F32.wireOp",EDGE,"E41"),sQuery(id+"F32.wireOp",EDGE,"E42"),sQuery(id+"F32.wireOp",EDGE,"E43")])],"isStart":false})],"blendedInto":[makeQuery(id+"F33.opExtrude","CAP_FACE",FACE,{"disambiguationData":[OSD([sQuery(id+"F32.wireOp",EDGE,"E32"),subQ1,subQ0,sQuery(id+"F32.wireOp",EDGE,"E37"),sQuery(id+"F32.wireOp",EDGE,"E38"),sQuery(id+"F32.wireOp",EDGE,"E40"),sQuery(id+"F32.wireOp",EDGE,"E41"),sQuery(id+"F32.wireOp",EDGE,"E42"),sQuery(id+"F32.wireOp",EDGE,"E43")])],"isStart":false})]});}
            var Q1;
            {var subQ0=sQuery(id+"F32.wireOp",EDGE,"E37");Q1=makeQuery(id+"F34.opFillet","BLEND_EDGE",EDGE,{"blendedFrom":[makeQuery(id+"F33.opExtrude","SWEPT_EDGE",EDGE,{"disambiguationData":[OSD([sQuery(id+"F32.wireOp",EDGE,"E36"),subQ0])]}),makeQuery(id+"F33.opExtrude","CAP_EDGE",EDGE,{"disambiguationData":[OSD([subQ0])],"isStart":true})],"blendedInto":[]});}
            fillet(context, id + "F35", {"entities" : qUnion([Q0, Q1]), "radius" : 5.08 * mm, "tangentPropagation" : true, "allowEdgeOverflow" : false});
        }
        {
            var Q0;
            Q0=makeQuery(id+"F21.opExtrude","SWEPT_BODY",BODY,{"disambiguationData":[OSD([sQuery(id+"F20.wireOp",EDGE,"E19"),sQuery(id+"F20.wireOp",EDGE,"E21"),sQuery(id+"F20.wireOp",EDGE,"E22"),sQuery(id+"F20.wireOp",EDGE,"E20")])]});
            var Q1;
            Q1=makeQuery(id+"F30.opExtrude","SWEPT_BODY",BODY,{"disambiguationData":[OSD([sQuery(id+"F29.wireOp",EDGE,"E26"),sQuery(id+"F29.wireOp",EDGE,"E27"),sQuery(id+"F29.wireOp",EDGE,"E28")])]});
            var Q2;
            Q2=makeQuery(id+"F33.opExtrude","SWEPT_BODY",BODY,{"disambiguationData":[OSD([sQuery(id+"F32.wireOp",EDGE,"E32"),sQuery(id+"F32.wireOp",EDGE,"E35"),sQuery(id+"F32.wireOp",EDGE,"E36"),sQuery(id+"F32.wireOp",EDGE,"E37"),sQuery(id+"F32.wireOp",EDGE,"E38"),sQuery(id+"F32.wireOp",EDGE,"E40"),sQuery(id+"F32.wireOp",EDGE,"E41"),sQuery(id+"F32.wireOp",EDGE,"E42"),sQuery(id+"F32.wireOp",EDGE,"E43")])]});
            var Q3;
            Q3=qCreatedBy(makeId("Right.planeOp"),FACE);
            mirror(context, id + "F36", {"entities" : qUnion([Q0, Q1, Q2]), "mirrorPlane" : qUnion([Q3])});
        }
        {
            var Q0;
            Q0=makeQuery(id+"F7.opExtrude","SWEPT_BODY",BODY,{"disambiguationData":[OSD([sQuery(id+"F6.wireOp",EDGE,"E4"),sQuery(id+"F6.wireOp",EDGE,"E5")])]});
            var Q1;
            Q1=makeQuery(id+"F13.opExtrude","SWEPT_BODY",BODY,{"disambiguationData":[OSD([sQuery(id+"F12.wireOp",EDGE,"E16")])]});
            var Q2;
            Q2=makeQuery(id+"F14.opExtrude","SWEPT_BODY",BODY,{"disambiguationData":[OSD([sQuery(id+"F12.wireOp",EDGE,"E15"),sQuery(id+"F12.wireOp",EDGE,"E16")])]});
            var Q3;
            Q3=makeQuery(id+"F16.boolean.opBoolean","SPLIT",BODY,{"disambiguationData":[OD(0.0)],"derivedFrom":makeQuery(id+"F11.opExtrude","SWEPT_BODY",BODY,{"disambiguationData":[OSD([sQuery(id+"F10.wireOp",EDGE,"E7.0.0"),sQuery(id+"F10.wireOp",EDGE,"E7.0.1"),sQuery(id+"F10.wireOp",EDGE,"E7.0.2"),sQuery(id+"F10.wireOp",EDGE,"E7.0.3"),sQuery(id+"F10.wireOp",EDGE,"E14.bottom"),sQuery(id+"F10.wireOp",EDGE,"E14.top"),sQuery(id+"F10.wireOp",EDGE,"E14.left"),sQuery(id+"F10.wireOp",EDGE,"E14.right")])]})});
            var Q4;
            Q4=makeQuery(id+"F16.boolean.opBoolean","SPLIT",BODY,{"disambiguationData":[OD(1.0)],"derivedFrom":makeQuery(id+"F11.opExtrude","SWEPT_BODY",BODY,{"disambiguationData":[OSD([sQuery(id+"F10.wireOp",EDGE,"E7.0.0"),sQuery(id+"F10.wireOp",EDGE,"E7.0.1"),sQuery(id+"F10.wireOp",EDGE,"E7.0.2"),sQuery(id+"F10.wireOp",EDGE,"E7.0.3"),sQuery(id+"F10.wireOp",EDGE,"E14.bottom"),sQuery(id+"F10.wireOp",EDGE,"E14.top"),sQuery(id+"F10.wireOp",EDGE,"E14.left"),sQuery(id+"F10.wireOp",EDGE,"E14.right")])]})});
            var Q5;
            Q5=makeQuery(id+"F21.opExtrude","SWEPT_BODY",BODY,{"disambiguationData":[OSD([sQuery(id+"F20.wireOp",EDGE,"E19"),sQuery(id+"F20.wireOp",EDGE,"E21"),sQuery(id+"F20.wireOp",EDGE,"E22"),sQuery(id+"F20.wireOp",EDGE,"E20")])]});
            var Q6;
            Q6=makeQuery(id+"F24.opExtrude","SWEPT_BODY",BODY,{"disambiguationData":[OSD([sQuery(id+"F23.wireOp",EDGE,"E25.bottom"),sQuery(id+"F23.wireOp",EDGE,"E25.top"),sQuery(id+"F23.wireOp",EDGE,"E25.left"),sQuery(id+"F23.wireOp",EDGE,"E25.right")])]});
            var Q7;
            Q7=makeQuery(id+"F30.opExtrude","SWEPT_BODY",BODY,{"disambiguationData":[OSD([sQuery(id+"F29.wireOp",EDGE,"E26"),sQuery(id+"F29.wireOp",EDGE,"E27"),sQuery(id+"F29.wireOp",EDGE,"E28")])]});
            var Q8;
            Q8=makeQuery(id+"F33.opExtrude","SWEPT_BODY",BODY,{"disambiguationData":[OSD([sQuery(id+"F32.wireOp",EDGE,"E32"),sQuery(id+"F32.wireOp",EDGE,"E35"),sQuery(id+"F32.wireOp",EDGE,"E36"),sQuery(id+"F32.wireOp",EDGE,"E37"),sQuery(id+"F32.wireOp",EDGE,"E38"),sQuery(id+"F32.wireOp",EDGE,"E40"),sQuery(id+"F32.wireOp",EDGE,"E41"),sQuery(id+"F32.wireOp",EDGE,"E42"),sQuery(id+"F32.wireOp",EDGE,"E43")])]});
            var Q9;
            Q9=makeQuery(id+"F36.opPattern","COPY",BODY,{"derivedFrom":makeQuery(id+"F21.opExtrude","SWEPT_BODY",BODY,{"disambiguationData":[OSD([sQuery(id+"F20.wireOp",EDGE,"E19"),sQuery(id+"F20.wireOp",EDGE,"E21"),sQuery(id+"F20.wireOp",EDGE,"E22"),sQuery(id+"F20.wireOp",EDGE,"E20")])]}),"instanceName":"1"});
            var Q10;
            Q10=makeQuery(id+"F36.opPattern","COPY",BODY,{"derivedFrom":makeQuery(id+"F30.opExtrude","SWEPT_BODY",BODY,{"disambiguationData":[OSD([sQuery(id+"F29.wireOp",EDGE,"E26"),sQuery(id+"F29.wireOp",EDGE,"E27"),sQuery(id+"F29.wireOp",EDGE,"E28")])]}),"instanceName":"1"});
            var Q11;
            Q11=makeQuery(id+"F36.opPattern","COPY",BODY,{"derivedFrom":makeQuery(id+"F33.opExtrude","SWEPT_BODY",BODY,{"disambiguationData":[OSD([sQuery(id+"F32.wireOp",EDGE,"E32"),sQuery(id+"F32.wireOp",EDGE,"E35"),sQuery(id+"F32.wireOp",EDGE,"E36"),sQuery(id+"F32.wireOp",EDGE,"E37"),sQuery(id+"F32.wireOp",EDGE,"E38"),sQuery(id+"F32.wireOp",EDGE,"E40"),sQuery(id+"F32.wireOp",EDGE,"E41"),sQuery(id+"F32.wireOp",EDGE,"E42"),sQuery(id+"F32.wireOp",EDGE,"E43")])]}),"instanceName":"1"});
            var Q12;
            Q12=makeQuery(id+"F1.opExtrude","SWEPT_FACE",FACE,{"disambiguationData":[OSD([sQuery(id+"F0.wireOp",EDGE,"E0")])]});
            transform(context, id + "F37", {"entities" : qUnion([Q0, Q1, Q2, Q3, Q4, Q5, Q6, Q7, Q8, Q9, Q10, Q11]), "transformType" : TransformType.ROTATION, "transformAxis" : qUnion([Q12]), "angle" : 180 * degree, "makeCopy" : true});
        }
        {
            var Q0;
            Q0=qCreatedBy(makeId("Top.planeOp"),FACE);
            var sketch = newSketch(context, id + "F38", { "sketchPlane" : qUnion([Q0])});
            skCircle(sketch, "E44.0", {"center": v(0, 0) * mm, "radius": 50.8 * mm});
            skCircle(sketch, "E45.0", {"center": v(0, 0) * mm, "radius": 53.98 * mm});
            skSolve(sketch);
        }
        {
            var Q0;
            Q0=makeQuery(id+"F38.imprint","IMPRINT",FACE,{"disambiguationData":[TD([[makeQuery(id+"F38.imprint","IMPRINT",EDGE,{"derivedFrom":sQuery(id+"F38.wireOp",EDGE,"E44.0")}),-1.0]])]});
            extrude(context, id + "F39", {"entities" : qUnion([Q0]), "oppositeDirection" : true, "depth" : 6.35 * mm});
        }
        {
            var Q0;
            Q0=qCreatedBy(makeId("Right.planeOp"),FACE);
            var sketch = newSketch(context, id + "F40", { "sketchPlane" : qUnion([Q0])});
            skPoint(sketch, "E46.third.point", {"position": v(-138.86, 138.48) * mm});
            skLineSegment(sketch, "E47", {"start": v(-53.1, -6.4) * mm, "end": v(2.03, -6.3) * mm});
            skLineSegment(sketch, "E48", {"start": v(0, -6.31) * mm, "end": v(0, -17.48) * mm});
            skArc(sketch, "E49", {"start": v(-53.1, -6.4) * mm, "mid": v(-26.93, -13.79) * mm, "end": v(0, -17.48) * mm});
            skLineSegment(sketch, "E50.0", {"start": v(-53.98, 0) * mm, "end": v(53.98, 0) * mm});
            skLineSegment(sketch, "E51", {"start": v(0, 0) * mm, "end": v(0, -6.31) * mm});
            skSolve(sketch);
        }
        {
            var Q0;
            Q0=makeQuery(id+"F40.imprint","IMPRINT",FACE,{"disambiguationData":[TD([[makeQuery(id+"F40.imprint","IMPRINT",EDGE,{"derivedFrom":sQuery(id+"F40.wireOp",EDGE,"E47")}),-1.0]])]});
            var Q1;
            Q1=sQuery(id+"F40.wireOp",EDGE,"E48");
            revolve(context, id + "F41", {"entities" : qUnion([Q0]), "axis" : qUnion([Q1]), "revolveType" : RevolveType.FULL});
        }
        {
            var Q0;
            Q0=makeQuery(id+"F1.opExtrude","SWEPT_BODY",BODY,{"disambiguationData":[OSD([sQuery(id+"F0.wireOp",EDGE,"E0"),sQuery(id+"F0.wireOp",EDGE,"E1")])]});
            var Q1;
            Q1=makeQuery(id+"F4.opExtrude","SWEPT_BODY",BODY,{"disambiguationData":[OSD([sQuery(id+"F3.wireOp",EDGE,"E2"),sQuery(id+"F3.wireOp",EDGE,"E3")])]});
            var Q2;
            Q2=makeQuery(id+"F41.opRevolve","SWEPT_BODY",BODY,{"disambiguationData":[OSD([sQuery(id+"F40.wireOp",EDGE,"E46"),sQuery(id+"F40.wireOp",EDGE,"E47"),sQuery(id+"F40.wireOp",EDGE,"E48")])]});
            var Q3;
            Q3=makeQuery(id+"F39.opExtrude","SWEPT_BODY",BODY,{"disambiguationData":[OSD([sQuery(id+"F38.wireOp",EDGE,"E44.0"),sQuery(id+"F38.wireOp",EDGE,"E45.0")])]});
            var Q4;
            Q4=makeQuery(id+"F15.opFillet","BLEND_FACE",FACE,{"disambiguationData":[OSD([sQuery(id+"F12.wireOp",EDGE,"E16")])]});
            transform(context, id + "F42", {"entities" : qUnion([Q0, Q1, Q2, Q3]), "transformType" : TransformType.ROTATION, "transformAxis" : qUnion([Q4]), "angle" : 10 * degree, "makeCopy" : false});
        }
        {
            var Q0;
            Q0=qCreatedBy(makeId("Front.planeOp"),FACE);
            var sketch = newSketch(context, id + "F43", { "sketchPlane" : qUnion([Q0])});
            skArc(sketch, "E52", {"start": v(-50.73, 224.57) * mm, "mid": v(-8.09, 267.22) * mm, "end": v(-50.73, 309.87) * mm});
            skLineSegment(sketch, "E53", {"start": v(-50.73, 267.22) * mm, "end": v(-50.73, 224.57) * mm});
            skLineSegment(sketch, "E54", {"start": v(-50.73, 267.22) * mm, "end": v(-50.73, 309.87) * mm});
            skSolve(sketch);
        }
        {
            var Q0;
            Q0=makeQuery(id+"F43.imprint","IMPRINT",FACE,{"disambiguationData":[TD([[makeQuery(id+"F43.imprint","IMPRINT",EDGE,{"derivedFrom":sQuery(id+"F43.wireOp",EDGE,"E52")}),1.0]])]});
            var Q1;
            Q1=sQuery(id+"F43.wireOp",EDGE,"E54");
            revolve(context, id + "F44", {"entities" : qUnion([Q0]), "axis" : qUnion([Q1]), "revolveType" : RevolveType.FULL});
        }
        {
            var Q0;
            Q0=makeQuery(id+"F11.opExtrude","SWEPT_FACE",FACE,{"disambiguationData":[OSD([sQuery(id+"F10.wireOp",EDGE,"E14.top")])]});
            cPlane(context, id + "F45", {"entities" : qUnion([Q0]), "cplaneType" : CPlaneType.OFFSET, "offset" : 19.05 * mm, "oppositeDirection" : true, "width" : 152.4 * mm, "height" : 152.4 * mm});
        }
        {
            var Q0;
            Q0=qCreatedBy(id+"F45.planeOp",FACE);
            var sketch = newSketch(context, id + "F46", { "sketchPlane" : qUnion([Q0])});
            skLineSegment(sketch, "E55", {"start": v(0, 2.77) * mm, "end": v(0, 12.16) * mm});
            skCircle(sketch, "E56", {"center": v(0, 12.16) * mm, "radius": 6.35 * mm});
            skSolve(sketch);
        }
        {
            var Q0;
            Q0 = qSketchRegion(id + "F46", true);
            extrude(context, id + "F47", {"entities" : qUnion([Q0]), "operationType" : NewBodyOperationType.REMOVE, "depth" : 152.4 * mm});
        }
        {
            var Q0;
            Q0 = qSketchRegion(id + "F46", true);
            extrude(context, id + "F48", {"entities" : qUnion([Q0]), "depth" : 152.4 * mm});
        }
        {
            var Q0;
            Q0=makeQuery(id+"F1.opExtrude","CAP_FACE",FACE,{"disambiguationData":[OSD([sQuery(id+"F0.wireOp",EDGE,"E0"),sQuery(id+"F0.wireOp",EDGE,"E1")])],"isStart":false});
            cPlane(context, id + "F49", {"entities" : qUnion([Q0]), "cplaneType" : CPlaneType.OFFSET, "offset" : 105.92 * mm, "oppositeDirection" : true, "width" : 152.4 * mm, "height" : 152.4 * mm});
        }
        {
            var Q0;
            Q0=qCreatedBy(id+"F49.planeOp",FACE);
            var sketch = newSketch(context, id + "F50", { "sketchPlane" : qUnion([Q0])});
            skCircle(sketch, "E57.0", {"center": v(0, 0) * mm, "radius": 38.1 * mm});
            skSolve(sketch);
        }
        {
            var Q0;
            Q0=makeQuery(id+"F50.imprint","IMPRINT",FACE,{"disambiguationData":[TD([[makeQuery(id+"F50.imprint","IMPRINT",EDGE,{"derivedFrom":sQuery(id+"F50.wireOp",EDGE,"E57.0")}),1.0]])]});
            extrude(context, id + "F51", {"entities" : qUnion([Q0]), "depth" : 25.4 * mm});
        }
        {
            var Q0;
            Q0=makeQuery(id+"F37.opPattern","COPY",EDGE,{"derivedFrom":makeQuery(id+"F11.opExtrude","CAP_EDGE",EDGE,{"disambiguationData":[OSD([sQuery(id+"F10.wireOp",EDGE,"E14.left")])],"isStart":false}),"instanceName":"1"});
            cPlane(context, id + "F52", {"entities" : qUnion([Q0]), "cplaneType" : CPlaneType.LINE_ANGLE, "offset" : 25.4 * mm, "angle" : 100 * degree, "width" : 152.4 * mm, "height" : 152.4 * mm});
        }
        {
            var Q0;
            Q0=qCreatedBy(id+"F52.planeOp",FACE);
            var sketch = newSketch(context, id + "F53", { "sketchPlane" : qUnion([Q0])});
            skLineSegment(sketch, "E58.0.0", {"start": v(-38.1, 59.18) * mm, "end": v(38.1, 59.18) * mm});
            skLineSegment(sketch, "E59", {"start": v(0, 59.18) * mm, "end": v(0, 33.55) * mm});
            skCircle(sketch, "E60", {"center": v(0, 46.37) * mm, "radius": 6.48 * mm});
            skSolve(sketch);
        }
        {
            var Q0;
            {var subQ0=sQuery(id+"F53.wireOp",EDGE,"E60");var subQ1=sQuery(id+"F53.wireOp",EDGE,"E59");var subQ2=makeQuery(id+"F53.imprint","INTERSECT",VERTEX,{"disambiguationData":[OD(0.0)],"derivedFrom":[subQ1,subQ0]});Q0=makeQuery(id+"F53.imprint","IMPRINT",FACE,{"disambiguationData":[TD([[makeQuery(id+"F53.imprint","IMPRINT",EDGE,{"disambiguationData":[TD([[subQ2,1.0]])],"derivedFrom":subQ1}),-1.0]])]});}
            var Q1;
            {var subQ0=sQuery(id+"F53.wireOp",EDGE,"E60");var subQ1=sQuery(id+"F53.wireOp",EDGE,"E59");var subQ2=makeQuery(id+"F53.imprint","INTERSECT",VERTEX,{"disambiguationData":[OD(0.0)],"derivedFrom":[subQ1,subQ0]});Q1=makeQuery(id+"F53.imprint","IMPRINT",FACE,{"disambiguationData":[TD([[makeQuery(id+"F53.imprint","IMPRINT",EDGE,{"disambiguationData":[TD([[subQ2,1.0]])],"derivedFrom":subQ1}),1.0]])]});}
            extrude(context, id + "F54", {"entities" : qUnion([Q0, Q1]), "operationType" : NewBodyOperationType.REMOVE, "endBound" : BoundingType.THROUGH_ALL, "oppositeDirection" : true, "depth" : 25.4 * mm});
        }
        {
            var Q0;
            Q0=makeQuery(id+"F1.opExtrude","CAP_FACE",FACE,{"disambiguationData":[OSD([sQuery(id+"F0.wireOp",EDGE,"E0"),sQuery(id+"F0.wireOp",EDGE,"E1")])],"isStart":false});
            cPlane(context, id + "F55", {"entities" : qUnion([Q0]), "cplaneType" : CPlaneType.OFFSET, "offset" : 0 * mm, "width" : 152.4 * mm, "height" : 152.4 * mm});
        }
        {
            var Q0;
            Q0=qCreatedBy(id+"F55.planeOp",FACE);
            var sketch = newSketch(context, id + "F56", { "sketchPlane" : qUnion([Q0])});
            skCircle(sketch, "E61.0", {"center": v(0, 0) * mm, "radius": 38.1 * mm});
            skCircle(sketch, "E62.0", {"center": v(0, 0) * mm, "radius": 31.5 * mm});
            skSolve(sketch);
        }
        {
            var Q0;
            Q0=makeQuery(id+"F56.imprint","IMPRINT",FACE,{"disambiguationData":[TD([[makeQuery(id+"F56.imprint","IMPRINT",EDGE,{"derivedFrom":sQuery(id+"F56.wireOp",EDGE,"E61.0")}),1.0]])]});
            extrude(context, id + "F57", {"entities" : qUnion([Q0]), "operationType" : NewBodyOperationType.ADD, "oppositeDirection" : true, "depth" : 25.4 * mm});
        }
    });
